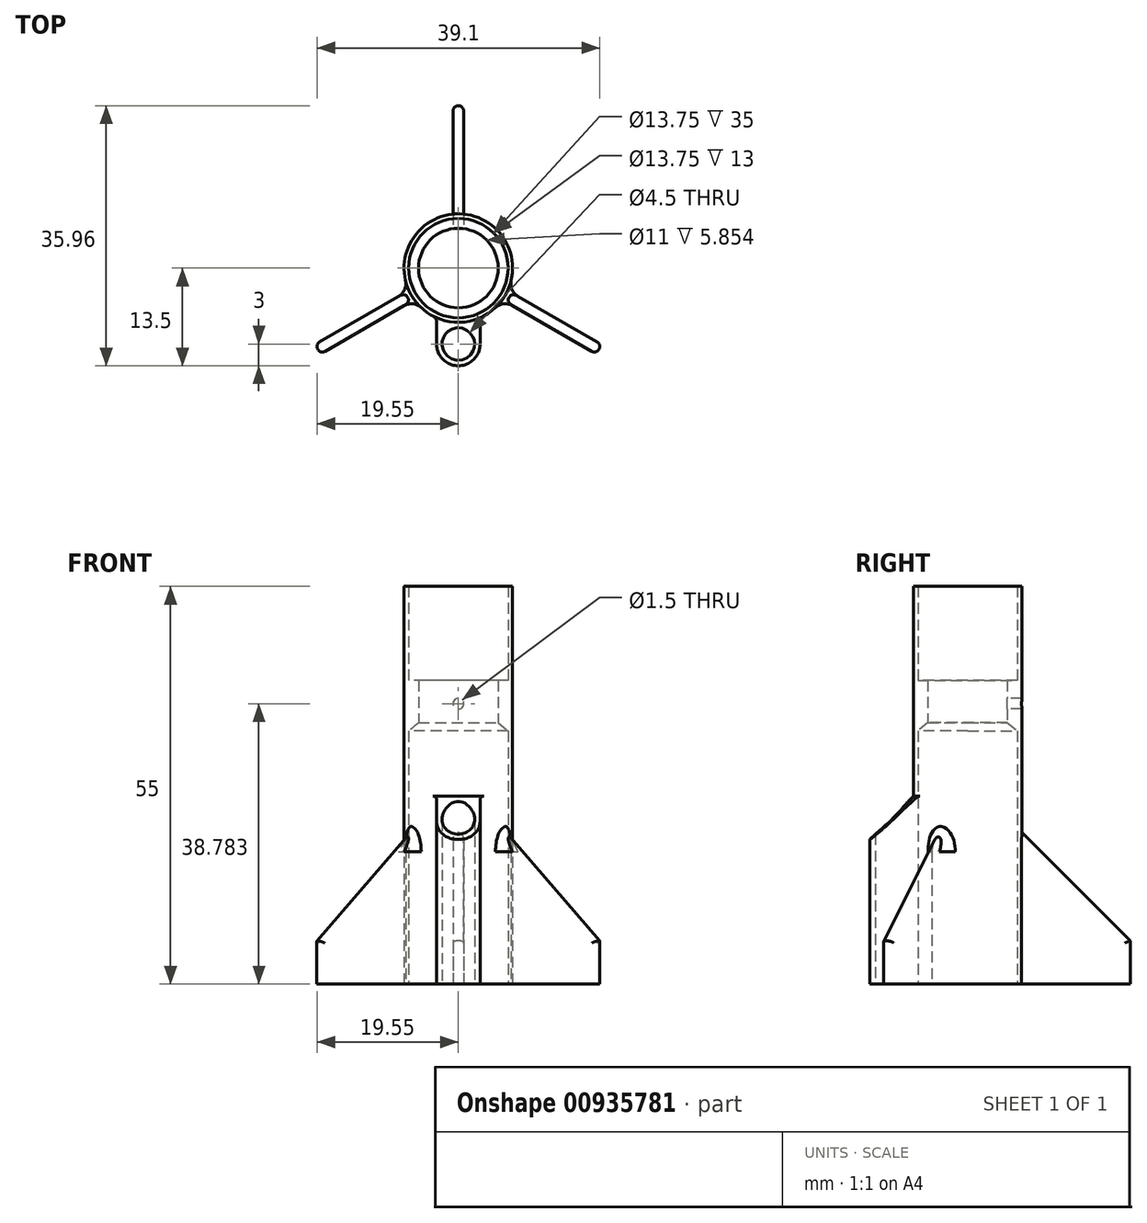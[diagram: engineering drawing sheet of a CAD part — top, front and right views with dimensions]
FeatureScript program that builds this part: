
annotation { "Feature Type Name" : "Feature", "Feature Type Description" : "" }
export const myFeature = defineFeature(function(context is Context, id is Id, definition is map)
    precondition{}
    {
        {
            var Q0;
            Q0=qCreatedBy(makeId("Top.planeOp"),FACE);
            var sketch = newSketch(context, id + "F0", { "sketchPlane" : qUnion([Q0])});
            skCircle(sketch, "E0", {"center": v(0, 0) * mm, "radius": 7.5 * mm});
            skCircle(sketch, "E1", {"center": v(0, 0) * mm, "radius": 6.88 * mm});
            skCircle(sketch, "E2", {"center": v(0, -10.5) * mm, "radius": 2.25 * mm});
            skCircle(sketch, "E3", {"center": v(0, -10.5) * mm, "radius": 3 * mm});
            skLineSegment(sketch, "E4", {"start": v(-3, -10.5) * mm, "end": v(-3, -6.87) * mm});
            skLineSegment(sketch, "E5", {"start": v(3, -10.5) * mm, "end": v(3, -6.87) * mm});
            skLineSegment(sketch, "E6.bottom", {"start": v(0.75, 22.46) * mm, "end": v(-0.75, 22.46) * mm});
            skLineSegment(sketch, "E6.top", {"start": v(0.75, 7.46) * mm, "end": v(-0.75, 7.46) * mm, "construction": true});
            skLineSegment(sketch, "E6.left", {"start": v(0.75, 22.46) * mm, "end": v(0.75, 7.46) * mm});
            skLineSegment(sketch, "E6.right", {"start": v(-0.75, 22.46) * mm, "end": v(-0.75, 7.46) * mm});
            skCircle(sketch, "E7", {"center": v(0, 0) * mm, "radius": 5.5 * mm});
            skSolve(sketch);
        }
        {
            var Q0;
            Q0=makeQuery(id+"F0.imprint","IMPRINT",FACE,{"disambiguationData":[TD([[makeQuery(id+"F0.imprint","IMPRINT",EDGE,{"derivedFrom":sQuery(id+"F0.wireOp",EDGE,"E1")}),-1.0]])]});
            var Q1;
            Q1=sQuery(id+"F0.wireOp",EDGE,"E0");
            var Q2;
            Q2=sQuery(id+"F0.wireOp",EDGE,"E1");
            extrude(context, id + "F1", {"entities" : qUnion([Q0]), "surfaceEntities" : qUnion([Q1, Q2]), "depth" : 55 * mm, "offsetDistance" : 25 * mm});
        }
        {
            var Q0;
            Q0=makeQuery(id+"F0.imprint","IMPRINT",FACE,{"disambiguationData":[TD([[makeQuery(id+"F0.imprint","IMPRINT",EDGE,{"derivedFrom":sQuery(id+"F0.wireOp",EDGE,"E6.bottom")}),1.0]])]});
            var Q1;
            {var subQ5=sQuery(id+"F0.wireOp",EDGE,"AX4Hb17H-Fm2N-gmPH-vryO-roIfLDdkge5b");Q1=makeQuery(id+"F0.imprint","IMPRINT",FACE,{"disambiguationData":[TD([[makeQuery(id+"F0.imprint","IMPRINT",EDGE,{"derivedFrom":subQ5}),-1.0]])]});}
            extrude(context, id + "F2", {"entities" : qUnion([Q0, Q1]), "operationType" : NewBodyOperationType.ADD, "depth" : 30 * mm, "offsetDistance" : 25 * mm});
        }
        {
            var Q0;
            Q0=makeQuery(id+"F2.opExtrude","CAP_EDGE",EDGE,{"disambiguationData":[OSD([sQuery(id+"F0.wireOp",EDGE,"E6.bottom")])],"isStart":false});
            chamfer(context, id + "F3", {"entities" : qUnion([Q0]), "width" : 24 * mm, "tangentPropagation" : true});
        }
        {
            var Q0;
            Q0=makeQuery(id+"F3.opChamfer","BLEND_EDGE",EDGE,{"blendedFrom":[makeQuery(id+"F2.opExtrude","CAP_EDGE",EDGE,{"disambiguationData":[OSD([sQuery(id+"F0.wireOp",EDGE,"E6.bottom")])],"isStart":false}),makeQuery(id+"F2.opExtrude","SWEPT_FACE",FACE,{"disambiguationData":[OSD([sQuery(id+"F0.wireOp",EDGE,"E6.left")])]})],"blendedInto":[makeQuery(id+"F2.opExtrude","SWEPT_FACE",FACE,{"disambiguationData":[OSD([sQuery(id+"F0.wireOp",EDGE,"E6.left")])]})]});
            var Q1;
            Q1=makeQuery(id+"F2.opExtrude","CAP_EDGE",EDGE,{"disambiguationData":[OSD([sQuery(id+"F0.wireOp",EDGE,"E6.left")])],"isStart":false});
            var Q2;
            Q2=makeQuery(id+"F3.opChamfer","BLEND_EDGE",EDGE,{"blendedFrom":[makeQuery(id+"F2.opExtrude","CAP_EDGE",EDGE,{"disambiguationData":[OSD([sQuery(id+"F0.wireOp",EDGE,"E6.bottom")])],"isStart":false}),makeQuery(id+"F2.opExtrude","SWEPT_FACE",FACE,{"disambiguationData":[OSD([sQuery(id+"F0.wireOp",EDGE,"E6.right")])]})],"blendedInto":[makeQuery(id+"F2.opExtrude","SWEPT_FACE",FACE,{"disambiguationData":[OSD([sQuery(id+"F0.wireOp",EDGE,"E6.right")])]})]});
            var Q3;
            Q3=makeQuery(id+"F2.opExtrude","CAP_EDGE",EDGE,{"disambiguationData":[OSD([sQuery(id+"F0.wireOp",EDGE,"E6.right")])],"isStart":false});
            var Q4;
            Q4=makeQuery(id+"F2.opExtrude","SWEPT_EDGE",EDGE,{"disambiguationData":[OSD([sQuery(id+"F0.wireOp",EDGE,"E6.bottom"),sQuery(id+"F0.wireOp",EDGE,"E6.left")])]});
            var Q5;
            Q5=makeQuery(id+"F2.opExtrude","SWEPT_EDGE",EDGE,{"disambiguationData":[OSD([sQuery(id+"F0.wireOp",EDGE,"E6.bottom"),sQuery(id+"F0.wireOp",EDGE,"E6.right")])]});
            fillet(context, id + "F4", {"entities" : qUnion([Q0, Q1, Q2, Q3, Q4, Q5]), "radius" : .75 * mm, "tangentPropagation" : true, "allowEdgeOverflow" : false});
        }
        {
            var Q0;
            Q0=makeQuery(id+"F1.opExtrude","SWEPT_BODY",BODY,{"disambiguationData":[OSD([sQuery(id+"F0.wireOp",EDGE,"E0"),sQuery(id+"F0.wireOp",EDGE,"E1")])]});
            var Q1;
            Q1=sQuery(id+"F0.wireOp",EDGE,"E0");
            circularPattern(context, id + "F5", {"entities" : qUnion([Q0]), "axis" : qUnion([Q1]), "angle" : 360 * degree, "instanceCount" : 3, "equalSpace" : true});
        }
        {
            var Q0;
            {var subQ0=sQuery(id+"F0.wireOp",EDGE,"E5");Q0=makeQuery(id+"F0.imprint","IMPRINT",FACE,{"disambiguationData":[TD([[makeQuery(id+"F0.imprint","IMPRINT",EDGE,{"derivedFrom":subQ0}),1.0]])]});}
            var Q1;
            {var subQ0=sQuery(id+"F0.wireOp",EDGE,"E4");Q1=makeQuery(id+"F0.imprint","IMPRINT",FACE,{"disambiguationData":[TD([[makeQuery(id+"F0.imprint","IMPRINT",EDGE,{"derivedFrom":subQ0}),-1.0]])]});}
            var Q2;
            Q2=makeQuery(id+"F0.imprint","IMPRINT",FACE,{"disambiguationData":[TD([[makeQuery(id+"F0.imprint","IMPRINT",EDGE,{"derivedFrom":sQuery(id+"F0.wireOp",EDGE,"E2")}),-1.0]])]});
            extrude(context, id + "F6", {"entities" : qUnion([Q0, Q1, Q2]), "operationType" : NewBodyOperationType.ADD, "depth" : 20 * mm, "offsetDistance" : 25 * mm});
        }
        {
            var Q0;
            {var subQ0=sQuery(id+"F0.wireOp",EDGE,"E0");var subQ1=makeQuery(id+"F1.opExtrude","SWEPT_FACE",FACE,{"disambiguationData":[OSD([subQ0])]});var subQ2=subQ1;Q0=makeQuery(id+"F6.boolean.opBoolean","INTERSECT",EDGE,{"disambiguationData":[topologyDisambiguationEdgeConnected([makeQuery(id+"F6.opExtrude","CAP_FACE",FACE,{"disambiguationData":[OSD([subQ0,sQuery(id+"F0.wireOp",EDGE,"E2"),sQuery(id+"F0.wireOp",EDGE,"E3"),sQuery(id+"F0.wireOp",EDGE,"E4"),sQuery(id+"F0.wireOp",EDGE,"E5")])],"isStart":false})])],"derivedFrom":[subQ2,makeQuery(id+"F5.opPattern","COPY",FACE,{"derivedFrom":subQ2,"instanceName":"1"}),makeQuery(id+"F5.opPattern","COPY",FACE,{"derivedFrom":subQ2,"instanceName":"2"})]});}
            chamfer(context, id + "F7", {"entities" : qUnion([Q0]), "width" : 6 * mm, "tangentPropagation" : true});
        }
        {
            var Q0;
            Q0=makeQuery(id+"F0.imprint","IMPRINT",FACE,{"disambiguationData":[TD([[makeQuery(id+"F0.imprint","IMPRINT",EDGE,{"derivedFrom":sQuery(id+"F0.wireOp",EDGE,"E1")}),1.0]])]});
            var Q1;
            Q1=sQuery(id+"F0.wireOp",EDGE,"E7");
            extrude(context, id + "F8", {"entities" : qUnion([Q0]), "operationType" : NewBodyOperationType.ADD, "surfaceEntities" : qUnion([Q1]), "depth" : 42 * mm, "offsetDistance" : 25 * mm, "hasSecondDirection" : true, "secondDirectionOppositeDirection" : false, "secondDirectionDepth" : 40 * mm});
        }
        {
            var Q0;
            Q0=makeQuery(id+"F8.opExtrude","CAP_EDGE",EDGE,{"disambiguationData":[OSD([sQuery(id+"F0.wireOp",EDGE,"E1")])],"isStart":true});
            chamfer(context, id + "F9", {"entities" : qUnion([Q0]), "chamferType" : ChamferType.TWO_OFFSETS, "width1" : 5 * mm, "oppositeDirection" : false, "width2" : 6 * mm, "tangentPropagation" : true});
        }
        {
            var Q0;
            {var subQ0=makeQuery(id+"F1.opExtrude","SWEPT_FACE",FACE,{"disambiguationData":[OSD([sQuery(id+"F0.wireOp",EDGE,"E0")])]});var subQ1=subQ0;Q0=makeQuery(id+"F6.boolean.opBoolean","INTERSECT",EDGE,{"disambiguationData":[topologyDisambiguationEdgeConnected([makeQuery(id+"F5.opPattern","COPY",FACE,{"derivedFrom":makeQuery(id+"F2.opExtrude","SWEPT_FACE",FACE,{"disambiguationData":[OSD([sQuery(id+"F0.wireOp",EDGE,"E6.left")])]}),"instanceName":"2"})])],"derivedFrom":[subQ1,makeQuery(id+"F5.opPattern","COPY",FACE,{"derivedFrom":subQ1,"instanceName":"1"})]});}
            var Q1;
            {var subQ0=makeQuery(id+"F1.opExtrude","SWEPT_FACE",FACE,{"disambiguationData":[OSD([sQuery(id+"F0.wireOp",EDGE,"E0")])]});var subQ1=subQ0;Q1=makeQuery(id+"F6.boolean.opBoolean","INTERSECT",EDGE,{"disambiguationData":[topologyDisambiguationEdgeConnected([makeQuery(id+"F5.opPattern","COPY",FACE,{"derivedFrom":makeQuery(id+"F2.opExtrude","SWEPT_FACE",FACE,{"disambiguationData":[OSD([sQuery(id+"F0.wireOp",EDGE,"E6.right")])]}),"instanceName":"1"})])],"derivedFrom":[subQ1,makeQuery(id+"F5.opPattern","COPY",FACE,{"derivedFrom":subQ1,"instanceName":"2"})]});}
            var Q2;
            Q2=makeQuery(id+"F2.opExtrude","SWEPT_EDGE",EDGE,{"disambiguationData":[OSD([sQuery(id+"F0.wireOp",EDGE,"E0"),sQuery(id+"F0.wireOp",EDGE,"E6.right")])]});
            fillet(context, id + "F10", {"entities" : qUnion([Q0, Q1, Q2]), "radius" : 2 * mm, "tangentPropagation" : true, "allowEdgeOverflow" : false});
        }
        {
            var Q0;
            {var subQ0=makeQuery(id+"F1.opExtrude","SWEPT_FACE",FACE,{"disambiguationData":[OSD([sQuery(id+"F0.wireOp",EDGE,"E0")])]});var subQ1=subQ0;Q0=makeQuery(id+"F6.boolean.opBoolean","INTERSECT",EDGE,{"disambiguationData":[topologyDisambiguationEdgeConnected([makeQuery(id+"F6.opExtrude","SWEPT_FACE",FACE,{"disambiguationData":[OSD([sQuery(id+"F0.wireOp",EDGE,"E5")])]})])],"derivedFrom":[subQ1,makeQuery(id+"F5.opPattern","COPY",FACE,{"derivedFrom":subQ1,"instanceName":"1"}),makeQuery(id+"F5.opPattern","COPY",FACE,{"derivedFrom":subQ1,"instanceName":"2"})]});}
            var Q1;
            {var subQ0=makeQuery(id+"F1.opExtrude","SWEPT_FACE",FACE,{"disambiguationData":[OSD([sQuery(id+"F0.wireOp",EDGE,"E0")])]});var subQ1=subQ0;Q1=makeQuery(id+"F6.boolean.opBoolean","INTERSECT",EDGE,{"disambiguationData":[topologyDisambiguationEdgeConnected([makeQuery(id+"F6.opExtrude","SWEPT_FACE",FACE,{"disambiguationData":[OSD([sQuery(id+"F0.wireOp",EDGE,"E4")])]})])],"derivedFrom":[subQ1,makeQuery(id+"F5.opPattern","COPY",FACE,{"derivedFrom":subQ1,"instanceName":"1"}),makeQuery(id+"F5.opPattern","COPY",FACE,{"derivedFrom":subQ1,"instanceName":"2"})]});}
            fillet(context, id + "F11", {"entities" : qUnion([Q0, Q1]), "radius" : 1 * mm, "tangentPropagation" : true, "allowEdgeOverflow" : false});
        }
        {
            var Q0;
            Q0=qCreatedBy(makeId("Front.planeOp"),FACE);
            var sketch = newSketch(context, id + "F12", { "sketchPlane" : qUnion([Q0])});
            skCircle(sketch, "E8", {"center": v(0, 38.78) * mm, "radius": 0.75 * mm});
            skSolve(sketch);
        }
        {
            var Q0;
            Q0 = qSketchRegion(id + "F12", true);
            extrude(context, id + "F13", {"entities" : qUnion([Q0]), "operationType" : NewBodyOperationType.REMOVE, "oppositeDirection" : true, "depth" : 25 * mm, "offsetDistance" : 25 * mm});
        }
    });
